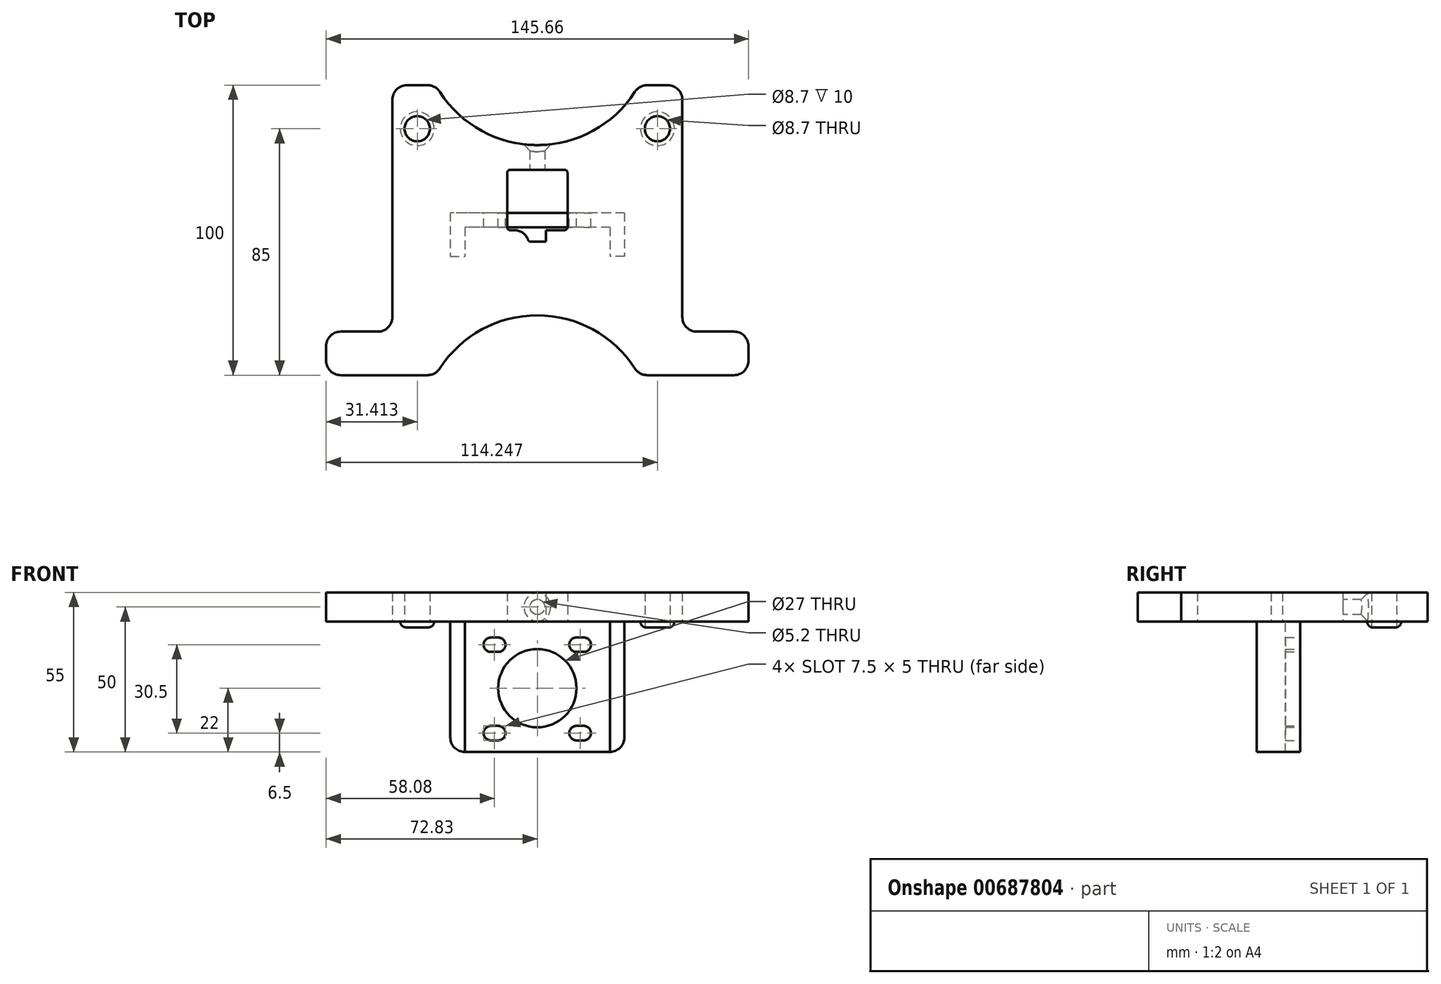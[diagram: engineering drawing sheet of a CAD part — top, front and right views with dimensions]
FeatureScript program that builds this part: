
annotation { "Feature Type Name" : "Feature", "Feature Type Description" : "" }
export const myFeature = defineFeature(function(context is Context, id is Id, definition is map)
    precondition{}
    {
        {
            var Q0;
            Q0=qCreatedBy(makeId("Top.planeOp"),FACE);
            var sketch = newSketch(context, id + "F0", { "sketchPlane" : qUnion([Q0])});
            skLineSegment(sketch, "E0.bottom", {"start": v(-10.4, 20.8) * mm, "end": v(10.4, 20.8) * mm});
            skLineSegment(sketch, "E0.top", {"start": v(-10.4, 0) * mm, "end": v(10.4, 0) * mm});
            skLineSegment(sketch, "E0.left", {"start": v(-10.4, 20.8) * mm, "end": v(-10.4, 0) * mm});
            skLineSegment(sketch, "E0.right", {"start": v(10.4, 20.8) * mm, "end": v(10.4, 0) * mm});
            skLineSegment(sketch, "E1.bottom", {"start": v(-45, 50) * mm, "end": v(-37.83, 50) * mm});
            skLineSegment(sketch, "E1.left", {"start": v(-50, 45) * mm, "end": v(-50, -30) * mm});
            skLineSegment(sketch, "E1.right", {"start": v(50, 45) * mm, "end": v(50, -30) * mm});
            skArc(sketch, "E2", {"start": v(-33.63, 47.7) * mm, "mid": v(0, 29.36) * mm, "end": v(33.63, 47.7) * mm});
            skPoint(sketch, "E3.visualSharp", {"position": v(-50, 50) * mm});
            skArc(sketch, "E3.filletArc", {"start": v(-45, 50) * mm, "mid": v(-48.54, 48.54) * mm, "end": v(-50, 45) * mm});
            skPoint(sketch, "E4.visualSharp", {"position": v(50, 50) * mm});
            skArc(sketch, "E4.filletArc", {"start": v(50, 45) * mm, "mid": v(48.54, 48.54) * mm, "end": v(45, 50) * mm});
            skLineSegment(sketch, "E5.trimOffspring", {"start": v(37.83, 50) * mm, "end": v(45, 50) * mm});
            skPoint(sketch, "E6.visualSharp", {"position": v(-35, 50) * mm});
            skArc(sketch, "E6.filletArc", {"start": v(-33.63, 47.7) * mm, "mid": v(-35.44, 49.39) * mm, "end": v(-37.83, 50) * mm});
            skPoint(sketch, "E7.visualSharp", {"position": v(35, 50) * mm});
            skArc(sketch, "E7.filletArc", {"start": v(37.83, 50) * mm, "mid": v(35.44, 49.39) * mm, "end": v(33.63, 47.7) * mm});
            skArc(sketch, "E8.MirrorCS", {"start": v(-33.63, -47.7) * mm, "mid": v(0, -29.36) * mm, "end": v(33.63, -47.7) * mm});
            skPoint(sketch, "E9.MirrorP", {"position": v(35, -50) * mm});
            skArc(sketch, "E10.MirrorCS", {"start": v(37.83, -50) * mm, "mid": v(35.44, -49.39) * mm, "end": v(33.63, -47.7) * mm});
            skArc(sketch, "E11.MirrorCS", {"start": v(-33.63, -47.7) * mm, "mid": v(-35.44, -49.39) * mm, "end": v(-37.83, -50) * mm});
            skCircle(sketch, "E12", {"center": v(-41.42, 35) * mm, "radius": 4.35 * mm});
            skPoint(sketch, "E12.centerSnap0", {"position": v(-41.42, 50) * mm});
            skCircle(sketch, "E13.MirrorC", {"center": v(41.42, 35) * mm, "radius": 4.35 * mm});
            skLineSegment(sketch, "E14.top", {"start": v(55, -35) * mm, "end": v(67.83, -35) * mm});
            skLineSegment(sketch, "E14.right", {"start": v(72.83, -45) * mm, "end": v(72.83, -40) * mm});
            skPoint(sketch, "E15.orphan", {"position": v(50, -45) * mm});
            skPoint(sketch, "E16.visualSharp", {"position": v(50, -35) * mm});
            skArc(sketch, "E16.filletArc", {"start": v(50, -30) * mm, "mid": v(51.46, -33.54) * mm, "end": v(55, -35) * mm});
            skPoint(sketch, "E17.visualSharp", {"position": v(72.83, -35) * mm});
            skArc(sketch, "E17.filletArc", {"start": v(72.83, -40) * mm, "mid": v(71.37, -36.46) * mm, "end": v(67.83, -35) * mm});
            skPoint(sketch, "E18.visualSharp", {"position": v(72.83, -50) * mm});
            skArc(sketch, "E18.filletArc", {"start": v(67.83, -50) * mm, "mid": v(71.37, -48.54) * mm, "end": v(72.83, -45) * mm});
            skArc(sketch, "E19.MirrorCS", {"start": v(-50, -30) * mm, "mid": v(-51.46, -33.54) * mm, "end": v(-55, -35) * mm});
            skLineSegment(sketch, "E20.MirrorCS", {"start": v(-55, -35) * mm, "end": v(-67.83, -35) * mm});
            skArc(sketch, "E21.MirrorCS", {"start": v(-72.83, -40) * mm, "mid": v(-71.37, -36.46) * mm, "end": v(-67.83, -35) * mm});
            skLineSegment(sketch, "E22.MirrorCS", {"start": v(-72.83, -45) * mm, "end": v(-72.83, -40) * mm});
            skArc(sketch, "E23.MirrorCS", {"start": v(-67.83, -50) * mm, "mid": v(-71.37, -48.54) * mm, "end": v(-72.83, -45) * mm});
            skLineSegment(sketch, "E24", {"start": v(-67.83, -50) * mm, "end": v(-37.83, -50) * mm});
            skLineSegment(sketch, "E25", {"start": v(37.83, -50) * mm, "end": v(67.83, -50) * mm});
            skSolve(sketch);
        }
        {
            var Q0;
            Q0=makeQuery(id+"F0.imprint","IMPRINT",FACE,{"disambiguationData":[TD([[makeQuery(id+"F0.imprint","IMPRINT",EDGE,{"derivedFrom":sQuery(id+"F0.wireOp",EDGE,"E0.bottom")}),1.0]])]});
            extrude(context, id + "F1", {"entities" : qUnion([Q0]), "depth" : 10 * mm, "offsetDistance" : 25 * mm});
        }
        {
            var Q0;
            Q0=makeQuery(id+"F1.opExtrude","CAP_FACE",FACE,{"disambiguationData":[OSD([sQuery(id+"F0.wireOp",EDGE,"E0.bottom"),sQuery(id+"F0.wireOp",EDGE,"E0.top"),sQuery(id+"F0.wireOp",EDGE,"E0.left"),sQuery(id+"F0.wireOp",EDGE,"E0.right"),sQuery(id+"F0.wireOp",EDGE,"E1.bottom"),sQuery(id+"F0.wireOp",EDGE,"E1.top"),sQuery(id+"F0.wireOp",EDGE,"E1.left"),sQuery(id+"F0.wireOp",EDGE,"E1.right"),sQuery(id+"F0.wireOp",EDGE,"E2"),sQuery(id+"F0.wireOp",EDGE,"E3.filletArc"),sQuery(id+"F0.wireOp",EDGE,"E4.filletArc"),sQuery(id+"F0.wireOp",EDGE,"E5.trimOffspring"),sQuery(id+"F0.wireOp",EDGE,"E6.filletArc"),sQuery(id+"F0.wireOp",EDGE,"E7.filletArc"),sQuery(id+"F0.wireOp",EDGE,"E8.MirrorCS"),sQuery(id+"F0.wireOp",EDGE,"E10.MirrorCS"),sQuery(id+"F0.wireOp",EDGE,"E11.MirrorCS"),sQuery(id+"F0.wireOp",EDGE,"77618663-be0e-429a-ab32-8c8d7f4d8b2e0.MirrorCS"),sQuery(id+"F0.wireOp",EDGE,"efaac38b-90d6-4923-b91b-45cde87492590.MirrorCS"),sQuery(id+"F0.wireOp",EDGE,"5d24c85b-4062-48f7-95b7-0e1149f7353b.trimOffspring"),sQuery(id+"F0.wireOp",EDGE,"E12"),sQuery(id+"F0.wireOp",EDGE,"E13.MirrorC")])],"isStart":true});
            var sketch = newSketch(context, id + "F2", { "sketchPlane" : qUnion([Q0])});
            skLineSegment(sketch, "E26.bottom", {"start": v(30, -6) * mm, "end": v(-30, -6) * mm});
            skLineSegment(sketch, "E26.top", {"start": v(25, -1) * mm, "end": v(-25, -1) * mm});
            skLineSegment(sketch, "E26.left", {"start": v(30, -6) * mm, "end": v(30, -1) * mm});
            skLineSegment(sketch, "E26.right", {"start": v(-30, -6) * mm, "end": v(-30, -1) * mm});
            skLineSegment(sketch, "E27.top", {"start": v(30, 9) * mm, "end": v(25, 9) * mm});
            skLineSegment(sketch, "E27.left", {"start": v(30, -1) * mm, "end": v(30, 9) * mm});
            skLineSegment(sketch, "E27.right", {"start": v(25, -1) * mm, "end": v(25, 9) * mm});
            skLineSegment(sketch, "E28.top", {"start": v(-30, 9) * mm, "end": v(-25, 9) * mm});
            skLineSegment(sketch, "E28.left", {"start": v(-30, -1) * mm, "end": v(-30, 9) * mm});
            skLineSegment(sketch, "E28.right", {"start": v(-25, -1) * mm, "end": v(-25, 9) * mm});
            skSolve(sketch);
        }
        {
            var Q0;
            {var subQ0=sQuery(id+"F2.wireOp",EDGE,"E26.left");Q0=makeQuery(id+"F2.imprint","IMPRINT",FACE,{"disambiguationData":[TD([[makeQuery(id+"F2.imprint","IMPRINT",EDGE,{"derivedFrom":subQ0}),1.0]])]});}
            var Q1;
            {var subQ0=sQuery(id+"F2.wireOp",EDGE,"E26.bottom");var subQ1=makeQuery(id+"F1.opExtrude","CAP_EDGE",EDGE,{"disambiguationData":[OSD([sQuery(id+"F0.wireOp",EDGE,"E0.right")])],"isStart":true});var subQ2=makeQuery(id+"F2.imprint","INTERSECT",VERTEX,{"derivedFrom":[subQ1,subQ0]});Q1=makeQuery(id+"F2.imprint","IMPRINT",FACE,{"disambiguationData":[TD([[makeQuery(id+"F2.imprint","IMPRINT",EDGE,{"disambiguationData":[TD([[subQ2,-1.0]])],"derivedFrom":subQ0}),-1.0]])]});}
            var Q2;
            {var subQ0=sQuery(id+"F2.wireOp",EDGE,"E26.right");Q2=makeQuery(id+"F2.imprint","IMPRINT",FACE,{"disambiguationData":[TD([[makeQuery(id+"F2.imprint","IMPRINT",EDGE,{"derivedFrom":subQ0}),-1.0]])]});}
            extrude(context, id + "F3", {"entities" : qUnion([Q0, Q1, Q2]), "operationType" : NewBodyOperationType.ADD, "depth" : 45 * mm, "offsetDistance" : 25 * mm});
        }
        {
            var Q0;
            Q0=makeQuery(id+"F3.opExtrude","SWEPT_FACE",FACE,{"disambiguationData":[OSD([sQuery(id+"F2.wireOp",EDGE,"E26.bottom")])]});
            var sketch = newSketch(context, id + "F4", { "sketchPlane" : qUnion([Q0])});
            skCircle(sketch, "E29", {"center": v(0, -23) * mm, "radius": 13.5 * mm});
            skPoint(sketch, "E29.centerSnap0", {"position": v(-0.8, 0.2) * mm});
            skArc(sketch, "E30", {"start": v(-16, -5.5) * mm, "mid": v(-18.5, -8) * mm, "end": v(-16, -10.5) * mm});
            skArc(sketch, "E31.0.1.0", {"start": v(-16, -36) * mm, "mid": v(-18.5, -38.5) * mm, "end": v(-16, -41) * mm});
            skArc(sketch, "E31.1.0.0", {"start": v(16, -10.5) * mm, "mid": v(18.5, -8) * mm, "end": v(16, -5.5) * mm});
            skArc(sketch, "E31.1.1.0", {"start": v(16, -41) * mm, "mid": v(18.5, -38.5) * mm, "end": v(16, -36) * mm});
            skLineSegment(sketch, "E31.direction1", {"start": v(-16, -8) * mm, "end": v(16, -8) * mm, "construction": true});
            skLineSegment(sketch, "E31.direction2", {"start": v(-16, -8) * mm, "end": v(-16, -38.5) * mm, "construction": true});
            skLineSegment(sketch, "E32", {"start": v(-24.8, -41.58) * mm, "end": v(23.2, -41.58) * mm, "construction": true});
            skArc(sketch, "E33", {"start": v(13.5, -36) * mm, "mid": v(11, -38.5) * mm, "end": v(13.5, -41) * mm});
            skArc(sketch, "E34", {"start": v(13.5, -5.5) * mm, "mid": v(11, -8) * mm, "end": v(13.5, -10.5) * mm});
            skArc(sketch, "E35", {"start": v(-13.5, -10.5) * mm, "mid": v(-11, -8) * mm, "end": v(-13.5, -5.5) * mm});
            skPoint(sketch, "E36.center.orphan", {"position": v(-20.3, -38.5) * mm});
            skArc(sketch, "E37", {"start": v(-13.5, -41) * mm, "mid": v(-11, -38.5) * mm, "end": v(-13.5, -36) * mm});
            skLineSegment(sketch, "E38", {"start": v(-16, -36) * mm, "end": v(-13.5, -36) * mm});
            skLineSegment(sketch, "E39", {"start": v(-16, -41) * mm, "end": v(-13.5, -41) * mm});
            skLineSegment(sketch, "E40", {"start": v(13.5, -36) * mm, "end": v(16, -36) * mm});
            skLineSegment(sketch, "E41", {"start": v(13.5, -41) * mm, "end": v(16, -41) * mm});
            skLineSegment(sketch, "E42", {"start": v(-16, -5.5) * mm, "end": v(-13.5, -5.5) * mm});
            skLineSegment(sketch, "E43", {"start": v(-16, -10.5) * mm, "end": v(-13.5, -10.5) * mm});
            skLineSegment(sketch, "E44", {"start": v(13.5, -5.5) * mm, "end": v(16, -5.5) * mm});
            skLineSegment(sketch, "E45", {"start": v(13.5, -10.5) * mm, "end": v(16, -10.5) * mm});
            skSolve(sketch);
        }
        {
            var Q0;
            Q0=makeQuery(id+"F4.imprint","IMPRINT",FACE,{"disambiguationData":[TD([[makeQuery(id+"F4.imprint","IMPRINT",EDGE,{"derivedFrom":sQuery(id+"F4.wireOp",EDGE,"E29")}),1.0]])]});
            var Q1;
            Q1=makeQuery(id+"F4.imprint","IMPRINT",FACE,{"disambiguationData":[TD([[makeQuery(id+"F4.imprint","IMPRINT",EDGE,{"derivedFrom":sQuery(id+"F4.wireOp",EDGE,"E31.0.1.0")}),1.0]])]});
            var Q2;
            Q2=makeQuery(id+"F4.imprint","IMPRINT",FACE,{"disambiguationData":[TD([[makeQuery(id+"F4.imprint","IMPRINT",EDGE,{"derivedFrom":sQuery(id+"F4.wireOp",EDGE,"E31.1.1.0")}),1.0]])]});
            var Q3;
            Q3=makeQuery(id+"F4.imprint","IMPRINT",FACE,{"disambiguationData":[TD([[makeQuery(id+"F4.imprint","IMPRINT",EDGE,{"derivedFrom":sQuery(id+"F4.wireOp",EDGE,"E31.1.0.0")}),1.0]])]});
            var Q4;
            Q4=makeQuery(id+"F4.imprint","IMPRINT",FACE,{"disambiguationData":[TD([[makeQuery(id+"F4.imprint","IMPRINT",EDGE,{"derivedFrom":sQuery(id+"F4.wireOp",EDGE,"E30")}),1.0]])]});
            extrude(context, id + "F5", {"entities" : qUnion([Q0, Q1, Q2, Q3, Q4]), "operationType" : NewBodyOperationType.REMOVE, "oppositeDirection" : true, "depth" : 25 * mm, "offsetDistance" : 25 * mm});
        }
        {
            var Q0;
            Q0=makeQuery(id+"F3.opExtrude","CAP_EDGE",EDGE,{"disambiguationData":[OSD([sQuery(id+"F2.wireOp",EDGE,"E26.left")])],"isStart":false});
            var Q1;
            Q1=makeQuery(id+"F3.opExtrude","CAP_EDGE",EDGE,{"disambiguationData":[OSD([sQuery(id+"F2.wireOp",EDGE,"E26.right")])],"isStart":false});
            var Q2;
            Q2=makeQuery(id+"F3.opExtrude","CAP_EDGE",EDGE,{"disambiguationData":[OSD([sQuery(id+"F2.wireOp",EDGE,"E26.left")])],"isStart":true});
            var Q3;
            Q3=makeQuery(id+"F3.opExtrude","CAP_EDGE",EDGE,{"disambiguationData":[OSD([sQuery(id+"F2.wireOp",EDGE,"E26.right")])],"isStart":true});
            fillet(context, id + "F6", {"entities" : qUnion([Q0, Q1, Q2, Q3]), "radius" : 5 * mm, "tangentPropagation" : true, "allowEdgeOverflow" : false});
        }
        {
            var Q0;
            Q0=qCreatedBy(makeId("Front.planeOp"),FACE);
            var sketch = newSketch(context, id + "F7", { "sketchPlane" : qUnion([Q0])});
            skCircle(sketch, "E46", {"center": v(0, 5) * mm, "radius": 2.6 * mm});
            skSolve(sketch);
        }
        {
            var Q0;
            Q0=makeQuery(id+"F7.imprint","IMPRINT",FACE,{"disambiguationData":[TD([[makeQuery(id+"F7.imprint","IMPRINT",EDGE,{"derivedFrom":sQuery(id+"F7.wireOp",EDGE,"E46")}),1.0]])]});
            extrude(context, id + "F8", {"entities" : qUnion([Q0]), "operationType" : NewBodyOperationType.REMOVE, "oppositeDirection" : true, "depth" : 33 * mm, "offsetDistance" : 25 * mm});
        }
        {
            var Q0;
            Q0=makeQuery(id+"F8.boolean.opBoolean","INTERSECT",EDGE,{"derivedFrom":[makeQuery(id+"F1.opExtrude","SWEPT_FACE",FACE,{"disambiguationData":[OSD([sQuery(id+"F0.wireOp",EDGE,"E2")])]}),makeQuery(id+"F8.opExtrude","SWEPT_FACE",FACE,{"disambiguationData":[OSD([sQuery(id+"F7.wireOp",EDGE,"E46")])]})]});
            chamfer(context, id + "F9", {"entities" : qUnion([Q0]), "width" : 2.3 * mm, "tangentPropagation" : true});
        }
        {
            var Q0;
            Q0=makeQuery(id+"F1.opExtrude","CAP_FACE",FACE,{"disambiguationData":[OSD([sQuery(id+"F0.wireOp",EDGE,"E0.bottom"),sQuery(id+"F0.wireOp",EDGE,"E0.top"),sQuery(id+"F0.wireOp",EDGE,"E0.left"),sQuery(id+"F0.wireOp",EDGE,"E0.right"),sQuery(id+"F0.wireOp",EDGE,"E1.bottom"),sQuery(id+"F0.wireOp",EDGE,"E1.left"),sQuery(id+"F0.wireOp",EDGE,"E1.right"),sQuery(id+"F0.wireOp",EDGE,"E2"),sQuery(id+"F0.wireOp",EDGE,"E3.filletArc"),sQuery(id+"F0.wireOp",EDGE,"E4.filletArc"),sQuery(id+"F0.wireOp",EDGE,"E5.trimOffspring"),sQuery(id+"F0.wireOp",EDGE,"E6.filletArc"),sQuery(id+"F0.wireOp",EDGE,"E7.filletArc"),sQuery(id+"F0.wireOp",EDGE,"E8.MirrorCS"),sQuery(id+"F0.wireOp",EDGE,"E10.MirrorCS"),sQuery(id+"F0.wireOp",EDGE,"E11.MirrorCS"),sQuery(id+"F0.wireOp",EDGE,"E12"),sQuery(id+"F0.wireOp",EDGE,"E13.MirrorC"),sQuery(id+"F0.wireOp",EDGE,"E14.bottom"),sQuery(id+"F0.wireOp",EDGE,"E14.top"),sQuery(id+"F0.wireOp",EDGE,"E14.right"),sQuery(id+"F0.wireOp",EDGE,"E16.filletArc"),sQuery(id+"F0.wireOp",EDGE,"E17.filletArc"),sQuery(id+"F0.wireOp",EDGE,"E18.filletArc"),sQuery(id+"F0.wireOp",EDGE,"E19.MirrorCS"),sQuery(id+"F0.wireOp",EDGE,"E20.MirrorCS"),sQuery(id+"F0.wireOp",EDGE,"E21.MirrorCS"),sQuery(id+"F0.wireOp",EDGE,"E22.MirrorCS"),sQuery(id+"F0.wireOp",EDGE,"E23.MirrorCS"),sQuery(id+"F0.wireOp",EDGE,"95747fd1-36bf-4c4f-81a2-639faa3618470.MirrorCS")])],"isStart":true});
            var sketch = newSketch(context, id + "F10", { "sketchPlane" : qUnion([Q0])});
            skLineSegment(sketch, "E47.bottom", {"start": v(3, 0) * mm, "end": v(-3, 0) * mm});
            skLineSegment(sketch, "E47.top", {"start": v(3, 4) * mm, "end": v(-3, 4) * mm});
            skLineSegment(sketch, "E47.left", {"start": v(3, 0) * mm, "end": v(3, 4) * mm});
            skLineSegment(sketch, "E47.right", {"start": v(-3, 0) * mm, "end": v(-3, 4) * mm});
            skSolve(sketch);
        }
        {
            var Q0;
            Q0=makeQuery(id+"F10.imprint","IMPRINT",FACE,{"disambiguationData":[TD([[makeQuery(id+"F10.imprint","IMPRINT",EDGE,{"derivedFrom":sQuery(id+"F10.wireOp",EDGE,"E47.bottom")}),1.0]])]});
            extrude(context, id + "F11", {"entities" : qUnion([Q0]), "operationType" : NewBodyOperationType.REMOVE, "oppositeDirection" : true, "depth" : 25 * mm, "offsetDistance" : 25 * mm});
        }
        {
            var Q0;
            Q0=makeQuery(id+"F11.boolean.opBoolean","COPY",EDGE,{"derivedFrom":makeQuery(id+"F11.opExtrude","SWEPT_EDGE",EDGE,{"disambiguationData":[OSD([sQuery(id+"F0.wireOp",EDGE,"E0.top"),sQuery(id+"F10.wireOp",EDGE,"E47.bottom"),sQuery(id+"F10.wireOp",EDGE,"E47.left")])]})});
            var Q1;
            Q1=makeQuery(id+"F11.boolean.opBoolean","COPY",EDGE,{"derivedFrom":makeQuery(id+"F11.opExtrude","SWEPT_EDGE",EDGE,{"disambiguationData":[OSD([sQuery(id+"F0.wireOp",EDGE,"E0.top"),sQuery(id+"F10.wireOp",EDGE,"E47.bottom"),sQuery(id+"F10.wireOp",EDGE,"E47.right")])]})});
            fillet(context, id + "F12", {"entities" : qUnion([Q0, Q1]), "radius" : 5 * mm, "tangentPropagation" : true, "allowEdgeOverflow" : false});
        }
        {
            var Q0;
            Q0=makeQuery(id+"F1.opExtrude","SWEPT_EDGE",EDGE,{"disambiguationData":[OSD([sQuery(id+"F0.wireOp",EDGE,"E0.top"),sQuery(id+"F0.wireOp",EDGE,"E0.left")])]});
            var Q1;
            Q1=makeQuery(id+"F1.opExtrude","SWEPT_EDGE",EDGE,{"disambiguationData":[OSD([sQuery(id+"F0.wireOp",EDGE,"E0.top"),sQuery(id+"F0.wireOp",EDGE,"E0.right")])]});
            var Q2;
            Q2=makeQuery(id+"F1.opExtrude","SWEPT_EDGE",EDGE,{"disambiguationData":[OSD([sQuery(id+"F0.wireOp",EDGE,"E0.bottom"),sQuery(id+"F0.wireOp",EDGE,"E0.left")])]});
            var Q3;
            Q3=makeQuery(id+"F1.opExtrude","SWEPT_EDGE",EDGE,{"disambiguationData":[OSD([sQuery(id+"F0.wireOp",EDGE,"E0.bottom"),sQuery(id+"F0.wireOp",EDGE,"E0.right")])]});
            var Q4;
            Q4=makeQuery(id+"F12.opFillet","BLEND_EDGE",EDGE,{"blendedFrom":[makeQuery(id+"F11.boolean.opBoolean","COPY",EDGE,{"derivedFrom":makeQuery(id+"F11.opExtrude","SWEPT_EDGE",EDGE,{"disambiguationData":[OSD([sQuery(id+"F0.wireOp",EDGE,"E0.top"),sQuery(id+"F10.wireOp",EDGE,"E47.bottom"),sQuery(id+"F10.wireOp",EDGE,"E47.left")])]})}),makeQuery(id+"F11.boolean.opBoolean","COPY",FACE,{"derivedFrom":makeQuery(id+"F11.opExtrude","SWEPT_FACE",FACE,{"disambiguationData":[OSD([sQuery(id+"F10.wireOp",EDGE,"E47.top")])]})})],"blendedInto":[makeQuery(id+"F11.boolean.opBoolean","COPY",FACE,{"derivedFrom":makeQuery(id+"F11.opExtrude","SWEPT_FACE",FACE,{"disambiguationData":[OSD([sQuery(id+"F10.wireOp",EDGE,"E47.top")])]})})]});
            var Q5;
            Q5=makeQuery(id+"F12.opFillet","BLEND_EDGE",EDGE,{"blendedFrom":[makeQuery(id+"F11.boolean.opBoolean","COPY",EDGE,{"derivedFrom":makeQuery(id+"F11.opExtrude","SWEPT_EDGE",EDGE,{"disambiguationData":[OSD([sQuery(id+"F0.wireOp",EDGE,"E0.top"),sQuery(id+"F10.wireOp",EDGE,"E47.bottom"),sQuery(id+"F10.wireOp",EDGE,"E47.right")])]})}),makeQuery(id+"F11.boolean.opBoolean","COPY",FACE,{"derivedFrom":makeQuery(id+"F11.opExtrude","SWEPT_FACE",FACE,{"disambiguationData":[OSD([sQuery(id+"F10.wireOp",EDGE,"E47.top")])]})})],"blendedInto":[makeQuery(id+"F11.boolean.opBoolean","COPY",FACE,{"derivedFrom":makeQuery(id+"F11.opExtrude","SWEPT_FACE",FACE,{"disambiguationData":[OSD([sQuery(id+"F10.wireOp",EDGE,"E47.top")])]})})]});
            fillet(context, id + "F13", {"entities" : qUnion([Q0, Q1, Q2, Q3, Q4, Q5]), "radius" : 1 * mm, "tangentPropagation" : true, "allowEdgeOverflow" : false});
        }
        {
            var Q0;
            Q0=makeQuery(id+"F1.opExtrude","CAP_FACE",FACE,{"disambiguationData":[OSD([sQuery(id+"F0.wireOp",EDGE,"E0.bottom"),sQuery(id+"F0.wireOp",EDGE,"E0.top"),sQuery(id+"F0.wireOp",EDGE,"E0.left"),sQuery(id+"F0.wireOp",EDGE,"E0.right"),sQuery(id+"F0.wireOp",EDGE,"E1.bottom"),sQuery(id+"F0.wireOp",EDGE,"E1.left"),sQuery(id+"F0.wireOp",EDGE,"E1.right"),sQuery(id+"F0.wireOp",EDGE,"E2"),sQuery(id+"F0.wireOp",EDGE,"E3.filletArc"),sQuery(id+"F0.wireOp",EDGE,"E4.filletArc"),sQuery(id+"F0.wireOp",EDGE,"E5.trimOffspring"),sQuery(id+"F0.wireOp",EDGE,"E6.filletArc"),sQuery(id+"F0.wireOp",EDGE,"E7.filletArc"),sQuery(id+"F0.wireOp",EDGE,"E8.MirrorCS"),sQuery(id+"F0.wireOp",EDGE,"E10.MirrorCS"),sQuery(id+"F0.wireOp",EDGE,"E11.MirrorCS"),sQuery(id+"F0.wireOp",EDGE,"E12"),sQuery(id+"F0.wireOp",EDGE,"E13.MirrorC"),sQuery(id+"F0.wireOp",EDGE,"E14.top"),sQuery(id+"F0.wireOp",EDGE,"E14.right"),sQuery(id+"F0.wireOp",EDGE,"E16.filletArc"),sQuery(id+"F0.wireOp",EDGE,"E17.filletArc"),sQuery(id+"F0.wireOp",EDGE,"E18.filletArc"),sQuery(id+"F0.wireOp",EDGE,"E19.MirrorCS"),sQuery(id+"F0.wireOp",EDGE,"E20.MirrorCS"),sQuery(id+"F0.wireOp",EDGE,"E21.MirrorCS"),sQuery(id+"F0.wireOp",EDGE,"E22.MirrorCS"),sQuery(id+"F0.wireOp",EDGE,"E23.MirrorCS"),sQuery(id+"F0.wireOp",EDGE,"E24"),sQuery(id+"F0.wireOp",EDGE,"E25")])],"isStart":true});
            var sketch = newSketch(context, id + "F14", { "sketchPlane" : qUnion([Q0])});
            skCircle(sketch, "E48", {"center": v(41.42, -35) * mm, "radius": 5.85 * mm});
            skCircle(sketch, "E49", {"center": v(-41.42, -35) * mm, "radius": 5.85 * mm});
            skSolve(sketch);
        }
        {
            var Q0;
            Q0=makeQuery(id+"F14.imprint","IMPRINT",FACE,{"disambiguationData":[TD([[makeQuery(id+"F14.imprint","IMPRINT",EDGE,{"derivedFrom":sQuery(id+"F14.wireOp",EDGE,"E48")}),1.0]])]});
            var Q1;
            Q1=makeQuery(id+"F14.imprint","IMPRINT",FACE,{"disambiguationData":[TD([[makeQuery(id+"F14.imprint","IMPRINT",EDGE,{"derivedFrom":makeQuery(id+"F1.opExtrude","CAP_EDGE",EDGE,{"disambiguationData":[OSD([sQuery(id+"F0.wireOp",EDGE,"E13.MirrorC")])],"isStart":true})}),1.0]])]});
            var Q2;
            Q2=makeQuery(id+"F14.imprint","IMPRINT",FACE,{"disambiguationData":[TD([[makeQuery(id+"F14.imprint","IMPRINT",EDGE,{"derivedFrom":sQuery(id+"F14.wireOp",EDGE,"E49")}),1.0]])]});
            var Q3;
            Q3=makeQuery(id+"F14.imprint","IMPRINT",FACE,{"disambiguationData":[TD([[makeQuery(id+"F14.imprint","IMPRINT",EDGE,{"derivedFrom":makeQuery(id+"F1.opExtrude","CAP_EDGE",EDGE,{"disambiguationData":[OSD([sQuery(id+"F0.wireOp",EDGE,"E12")])],"isStart":true})}),-1.0]])]});
            extrude(context, id + "F15", {"entities" : qUnion([Q0, Q1, Q2, Q3]), "operationType" : NewBodyOperationType.ADD, "depth" : 2 * mm, "offsetDistance" : 25 * mm});
        }
        {
            var Q0;
            Q0=makeQuery(id+"F15.opExtrude","CAP_EDGE",EDGE,{"disambiguationData":[OSD([sQuery(id+"F14.wireOp",EDGE,"E48")])],"isStart":false});
            var Q1;
            Q1=makeQuery(id+"F15.opExtrude","CAP_EDGE",EDGE,{"disambiguationData":[OSD([sQuery(id+"F14.wireOp",EDGE,"E49")])],"isStart":false});
            var Q2;
            Q2=makeQuery(id+"F1.opExtrude","CAP_EDGE",EDGE,{"disambiguationData":[OSD([sQuery(id+"F0.wireOp",EDGE,"E12")])],"isStart":true});
            var Q3;
            Q3=makeQuery(id+"F1.opExtrude","CAP_EDGE",EDGE,{"disambiguationData":[OSD([sQuery(id+"F0.wireOp",EDGE,"E13.MirrorC")])],"isStart":true});
            fillet(context, id + "F16", {"entities" : qUnion([Q0, Q1, Q2, Q3]), "radius" : 2 * mm, "tangentPropagation" : true, "allowEdgeOverflow" : false});
        }
    });
